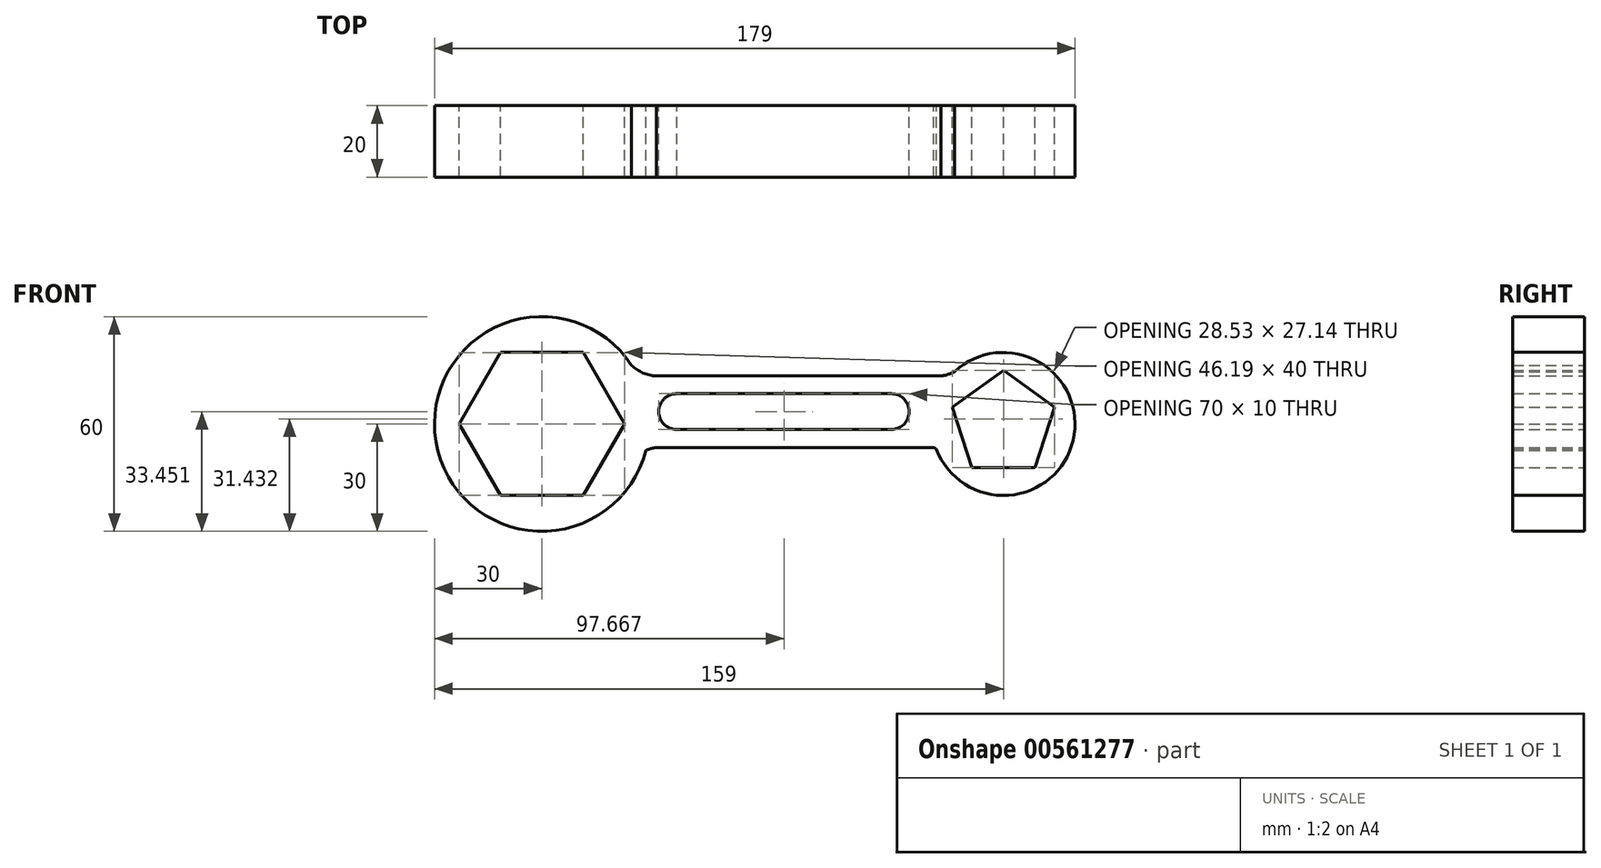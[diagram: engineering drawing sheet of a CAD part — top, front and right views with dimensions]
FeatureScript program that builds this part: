
annotation { "Feature Type Name" : "Feature", "Feature Type Description" : "" }
export const myFeature = defineFeature(function(context is Context, id is Id, definition is map)
    precondition{}
    {
        {
            var Q0;
            Q0=qCreatedBy(makeId("Front.planeOp"),FACE);
            var sketch = newSketch(context, id + "F0", { "sketchPlane" : qUnion([Q0])});
            skCircle(sketch, "E0.cCircle", {"center": v(0, 0) * mm, "radius": 12.14 * mm, "construction": true});
            skLineSegment(sketch, "E0.0", {"start": v(14.27, 4.64) * mm, "end": v(8.82, -12.14) * mm});
            skLineSegment(sketch, "E0.1", {"start": v(8.82, -12.14) * mm, "end": v(-8.82, -12.14) * mm});
            skLineSegment(sketch, "E0.2", {"start": v(-8.82, -12.14) * mm, "end": v(-14.27, 4.64) * mm});
            skLineSegment(sketch, "E0.3", {"start": v(-14.27, 4.64) * mm, "end": v(0, 15) * mm});
            skLineSegment(sketch, "E0.4", {"start": v(0, 15) * mm, "end": v(14.27, 4.64) * mm});
            skPoint(sketch, "E0.0.midPoint", {"position": v(11.54, -3.75) * mm});
            skCircle(sketch, "E1", {"center": v(0, 0) * mm, "radius": 20 * mm});
            skCircle(sketch, "E2.cCircle", {"center": v(-129, 0) * mm, "radius": 20 * mm, "construction": true});
            skLineSegment(sketch, "E2.0", {"start": v(-105.9, 0) * mm, "end": v(-117.45, -20) * mm});
            skLineSegment(sketch, "E2.1", {"start": v(-117.45, -20) * mm, "end": v(-140.55, -20) * mm});
            skLineSegment(sketch, "E2.2", {"start": v(-140.55, -20) * mm, "end": v(-152.1, 0) * mm});
            skLineSegment(sketch, "E2.3", {"start": v(-152.1, 0) * mm, "end": v(-140.55, 20) * mm});
            skLineSegment(sketch, "E2.4", {"start": v(-140.55, 20) * mm, "end": v(-117.45, 20) * mm});
            skLineSegment(sketch, "E2.5", {"start": v(-117.45, 20) * mm, "end": v(-105.9, 0) * mm});
            skPoint(sketch, "E2.0.midPoint", {"position": v(-111.68, -10) * mm});
            skCircle(sketch, "E3", {"center": v(-129, 0) * mm, "radius": 30 * mm});
            skLineSegment(sketch, "E4", {"start": v(-102.18, 13.45) * mm, "end": v(-14.8, 13.45) * mm});
            skLineSegment(sketch, "E5", {"start": v(-99.72, -6.55) * mm, "end": v(-18.9, -6.55) * mm});
            skLineSegment(sketch, "E6", {"start": v(-96.33, 3.45) * mm, "end": v(-96.33, 3.45) * mm});
            skLineSegment(sketch, "E7", {"start": v(-91.33, -1.55) * mm, "end": v(-31.33, -1.55) * mm});
            skLineSegment(sketch, "E8", {"start": v(-26.33, 1.55) * mm, "end": v(-26.33, 3.45) * mm});
            skPoint(sketch, "E9.visualSharp", {"position": v(-26.33, -1.55) * mm});
            skArc(sketch, "E9.filletArc", {"start": v(-31.33, -1.55) * mm, "mid": v(-27.8, -0.08) * mm, "end": v(-26.33, 3.45) * mm});
            skPoint(sketch, "E10.visualSharp", {"position": v(-26.33, 6.5) * mm});
            skPoint(sketch, "E11.visualSharp", {"position": v(-96.33, 8.5) * mm});
            skArc(sketch, "E11.filletArc", {"start": v(-91.28, 8.45) * mm, "mid": v(-94.85, 7) * mm, "end": v(-96.33, 3.45) * mm});
            skPoint(sketch, "E12.visualSharp", {"position": v(-96.33, -1.55) * mm});
            skArc(sketch, "E12.filletArc", {"start": v(-96.33, 3.45) * mm, "mid": v(-94.87, -0.08) * mm, "end": v(-91.33, -1.55) * mm});
            skLineSegment(sketch, "E13", {"start": v(-91.28, 8.45) * mm, "end": v(-31.33, 8.45) * mm});
            skLineSegment(sketch, "E14", {"start": v(-26.33, 3.45) * mm, "end": v(-26.33, 1.55) * mm});
            skPoint(sketch, "E15.visualSharp", {"position": v(-26.33, 8.45) * mm});
            skArc(sketch, "E15.filletArc", {"start": v(-26.33, 3.45) * mm, "mid": v(-27.8, 6.99) * mm, "end": v(-31.33, 8.45) * mm});
            skArc(sketch, "E16", {"start": v(-105.64, 18.82) * mm, "mid": v(-101.88, 14.85) * mm, "end": v(-96.6, 13.45) * mm});
            skArc(sketch, "E17", {"start": v(-96.6, -6.55) * mm, "mid": v(-103.95, -10.6) * mm, "end": v(-105.64, -18.82) * mm});
            skArc(sketch, "E18", {"start": v(-19.36, 13.45) * mm, "mid": v(-14.79, 14.09) * mm, "end": v(-10.99, 16.71) * mm});
            skArc(sketch, "E19", {"start": v(-17.15, -10.3) * mm, "mid": v(-19.2, -6.73) * mm, "end": v(-23.3, -6.55) * mm});
            skSolve(sketch);
        }
        {
            var Q0;
            Q0 = qSketchRegion(id + "F0", true);
            extrude(context, id + "F1", {"entities" : qUnion([Q0]), "depth" : 20 * mm, "offsetDistance" : 25 * mm});
        }
    });
